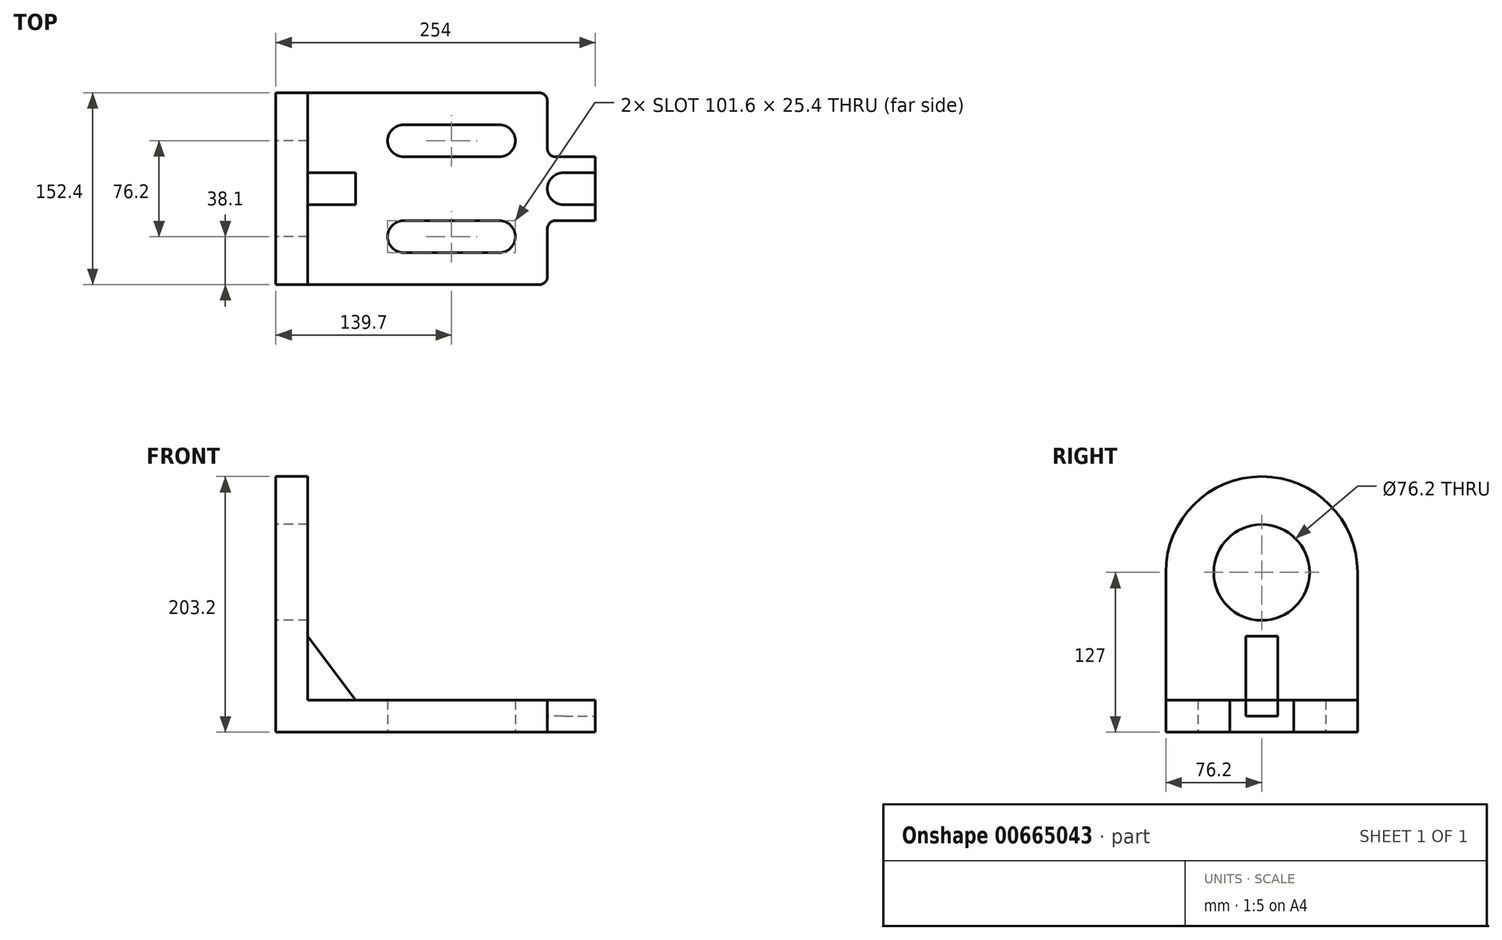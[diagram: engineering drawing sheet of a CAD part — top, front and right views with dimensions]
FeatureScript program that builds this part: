
annotation { "Feature Type Name" : "Feature", "Feature Type Description" : "" }
export const myFeature = defineFeature(function(context is Context, id is Id, definition is map)
    precondition{}
    {
        {
            var Q0;
            Q0=qCreatedBy(makeId("Top.planeOp"),FACE);
            var sketch = newSketch(context, id + "F0", { "sketchPlane" : qUnion([Q0])});
            skLineSegment(sketch, "E0", {"start": v(0, 0) * mm, "end": v(209.55, 0) * mm});
            skLineSegment(sketch, "E1", {"start": v(215.9, -6.35) * mm, "end": v(215.9, -44.45) * mm});
            skLineSegment(sketch, "E2", {"start": v(222.25, -50.8) * mm, "end": v(254, -50.8) * mm});
            skLineSegment(sketch, "E3", {"start": v(254, -50.8) * mm, "end": v(254, -63.5) * mm});
            skLineSegment(sketch, "E4", {"start": v(254, -63.5) * mm, "end": v(228.6, -63.5) * mm});
            skLineSegment(sketch, "E5", {"start": v(215.9, -76.2) * mm, "end": v(215.9, -76.2) * mm});
            skLineSegment(sketch, "E6", {"start": v(228.6, -88.9) * mm, "end": v(254, -88.9) * mm});
            skLineSegment(sketch, "E7", {"start": v(254, -88.9) * mm, "end": v(254, -101.6) * mm});
            skLineSegment(sketch, "E8", {"start": v(254, -101.6) * mm, "end": v(222.25, -101.6) * mm});
            skLineSegment(sketch, "E9", {"start": v(215.9, -107.95) * mm, "end": v(215.9, -146.05) * mm});
            skLineSegment(sketch, "E10", {"start": v(209.55, -152.4) * mm, "end": v(0, -152.4) * mm});
            skLineSegment(sketch, "E11", {"start": v(0, -152.4) * mm, "end": v(0, 0) * mm});
            skPoint(sketch, "E12.visualSharp", {"position": v(215.9, 0) * mm});
            skArc(sketch, "E12.filletArc", {"start": v(215.9, -6.35) * mm, "mid": v(214.04, -1.86) * mm, "end": v(209.55, 0) * mm});
            skPoint(sketch, "E13.visualSharp", {"position": v(215.9, -152.4) * mm});
            skArc(sketch, "E13.filletArc", {"start": v(209.55, -152.4) * mm, "mid": v(214.04, -150.54) * mm, "end": v(215.9, -146.05) * mm});
            skPoint(sketch, "E14.visualSharp", {"position": v(215.9, -50.8) * mm});
            skArc(sketch, "E14.filletArc", {"start": v(215.9, -44.45) * mm, "mid": v(217.76, -48.94) * mm, "end": v(222.25, -50.8) * mm});
            skPoint(sketch, "E15.visualSharp", {"position": v(215.9, -101.6) * mm});
            skArc(sketch, "E15.filletArc", {"start": v(222.25, -101.6) * mm, "mid": v(217.76, -103.46) * mm, "end": v(215.9, -107.95) * mm});
            skPoint(sketch, "E16.visualSharp", {"position": v(215.9, -63.5) * mm});
            skArc(sketch, "E16.filletArc", {"start": v(228.6, -63.5) * mm, "mid": v(219.62, -67.22) * mm, "end": v(215.9, -76.2) * mm});
            skPoint(sketch, "E17.visualSharp", {"position": v(215.9, -88.9) * mm});
            skArc(sketch, "E17.filletArc", {"start": v(215.9, -76.2) * mm, "mid": v(219.62, -85.18) * mm, "end": v(228.6, -88.9) * mm});
            skLineSegment(sketch, "E18", {"start": v(254, -63.5) * mm, "end": v(254, -88.9) * mm});
            skLineSegment(sketch, "E19.0", {"start": v(0, -38.1) * mm, "end": v(215.9, -38.1) * mm});
            skLineSegment(sketch, "E20.0", {"start": v(215.9, -114.3) * mm, "end": v(0, -114.3) * mm});
            skLineSegment(sketch, "E21.0", {"start": v(101.6, -50.8) * mm, "end": v(177.8, -50.8) * mm});
            skLineSegment(sketch, "E22.0", {"start": v(101.6, -25.4) * mm, "end": v(177.8, -25.4) * mm});
            skLineSegment(sketch, "E23.0", {"start": v(177.8, -101.6) * mm, "end": v(101.6, -101.6) * mm});
            skLineSegment(sketch, "E24.0", {"start": v(177.8, -127) * mm, "end": v(101.6, -127) * mm});
            skLineSegment(sketch, "E25.0", {"start": v(190.5, -38.1) * mm, "end": v(190.5, -38.1) * mm});
            skLineSegment(sketch, "E26.0", {"start": v(190.5, -114.3) * mm, "end": v(190.5, -114.3) * mm});
            skLineSegment(sketch, "E27.0", {"start": v(88.9, -38.1) * mm, "end": v(88.9, -38.1) * mm});
            skArc(sketch, "E28.filletArc", {"start": v(101.6, -25.4) * mm, "mid": v(92.62, -29.12) * mm, "end": v(88.9, -38.1) * mm});
            skArc(sketch, "E29.filletArc", {"start": v(88.9, -38.1) * mm, "mid": v(92.62, -47.08) * mm, "end": v(101.6, -50.8) * mm});
            skArc(sketch, "E30.filletArc", {"start": v(190.5, -38.1) * mm, "mid": v(186.78, -29.12) * mm, "end": v(177.8, -25.4) * mm});
            skPoint(sketch, "E31.visualSharp", {"position": v(190.5, -50.8) * mm});
            skArc(sketch, "E31.filletArc", {"start": v(177.8, -50.8) * mm, "mid": v(186.78, -47.08) * mm, "end": v(190.5, -38.1) * mm});
            skPoint(sketch, "E32.visualSharp", {"position": v(190.5, -101.6) * mm});
            skArc(sketch, "E32.filletArc", {"start": v(190.5, -114.3) * mm, "mid": v(186.78, -105.32) * mm, "end": v(177.8, -101.6) * mm});
            skArc(sketch, "E33.filletArc", {"start": v(177.8, -127) * mm, "mid": v(186.78, -123.28) * mm, "end": v(190.5, -114.3) * mm});
            skLineSegment(sketch, "E34", {"start": v(88.9, -114.3) * mm, "end": v(88.9, -114.3) * mm});
            skArc(sketch, "E35.filletArc", {"start": v(101.6, -101.6) * mm, "mid": v(92.62, -105.32) * mm, "end": v(88.9, -114.3) * mm});
            skArc(sketch, "E36.filletArc", {"start": v(88.9, -114.3) * mm, "mid": v(92.62, -123.28) * mm, "end": v(101.6, -127) * mm});
            skSolve(sketch);
        }
        {
            var Q0;
            Q0=makeQuery(id+"F0.imprint","IMPRINT",FACE,{"disambiguationData":[TD([[makeQuery(id+"F0.imprint","IMPRINT",EDGE,{"derivedFrom":sQuery(id+"F0.wireOp",EDGE,"E2")}),-1.0]])]});
            var Q1;
            {var subQ1=sQuery(id+"F0.wireOp",EDGE,"E0");Q1=makeQuery(id+"F0.imprint","IMPRINT",FACE,{"disambiguationData":[TD([[makeQuery(id+"F0.imprint","IMPRINT",EDGE,{"derivedFrom":subQ1}),-1.0]])]});}
            var Q2;
            {var subQ1=sQuery(id+"F0.wireOp",EDGE,"E10");Q2=makeQuery(id+"F0.imprint","IMPRINT",FACE,{"disambiguationData":[TD([[makeQuery(id+"F0.imprint","IMPRINT",EDGE,{"derivedFrom":subQ1}),-1.0]])]});}
            extrude(context, id + "F1", {"entities" : qUnion([Q0, Q1, Q2]), "depth" : 25.4 * mm, "offsetDistance" : 25.4 * mm});
        }
        {
            var Q0;
            Q0=makeQuery(id+"F0.imprint","IMPRINT",FACE,{"disambiguationData":[TD([[makeQuery(id+"F0.imprint","IMPRINT",EDGE,{"derivedFrom":sQuery(id+"F0.wireOp",EDGE,"E4")}),1.0]])]});
            extrude(context, id + "F2", {"entities" : qUnion([Q0]), "operationType" : NewBodyOperationType.ADD, "depth" : 12.7 * mm, "offsetDistance" : 25.4 * mm});
        }
        {
            var Q0;
            Q0=makeQuery(id+"F1.opExtrude","SWEPT_FACE",FACE,{"disambiguationData":[OSD([sQuery(id+"F0.wireOp",EDGE,"E11")])]});
            var sketch = newSketch(context, id + "F3", { "sketchPlane" : qUnion([Q0])});
            skLineSegment(sketch, "E37", {"start": v(0, 25.4) * mm, "end": v(0, 127) * mm});
            skLineSegment(sketch, "E38", {"start": v(76.2, 203.2) * mm, "end": v(76.2, 203.2) * mm});
            skLineSegment(sketch, "E39", {"start": v(152.4, 127) * mm, "end": v(152.4, 25.4) * mm});
            skPoint(sketch, "E40.visualSharp", {"position": v(0, 203.2) * mm});
            skArc(sketch, "E40.filletArc", {"start": v(76.2, 203.2) * mm, "mid": v(22.32, 180.88) * mm, "end": v(0, 127) * mm});
            skPoint(sketch, "E41.visualSharp", {"position": v(152.4, 203.2) * mm});
            skArc(sketch, "E41.filletArc", {"start": v(152.4, 127) * mm, "mid": v(130.08, 180.88) * mm, "end": v(76.2, 203.2) * mm});
            skCircle(sketch, "E42", {"center": v(76.2, 127) * mm, "radius": 38.1 * mm});
            skSolve(sketch);
        }
        {
            var Q0;
            Q0=makeQuery(id+"F3.imprint","IMPRINT",FACE,{"disambiguationData":[TD([[makeQuery(id+"F3.imprint","IMPRINT",EDGE,{"derivedFrom":sQuery(id+"F3.wireOp",EDGE,"E37")}),-1.0]])]});
            extrude(context, id + "F4", {"entities" : qUnion([Q0]), "operationType" : NewBodyOperationType.ADD, "oppositeDirection" : true, "depth" : 25.4 * mm, "offsetDistance" : 25.4 * mm});
        }
        {
            var Q0;
            Q0=makeQuery(id+"F4.boolean.opBoolean","MERGE",FACE,{"derivedFrom":[makeQuery(id+"F1.opExtrude","SWEPT_FACE",FACE,{"disambiguationData":[OSD([sQuery(id+"F0.wireOp",EDGE,"E10")])]}),makeQuery(id+"F4.opExtrude","SWEPT_FACE",FACE,{"disambiguationData":[OSD([sQuery(id+"F3.wireOp",EDGE,"E39")])]})]});
            var sketch = newSketch(context, id + "F5", { "sketchPlane" : qUnion([Q0])});
            skLineSegment(sketch, "E43", {"start": v(25.4, 25.4) * mm, "end": v(25.4, 76.2) * mm});
            skLineSegment(sketch, "E44", {"start": v(25.4, 25.4) * mm, "end": v(63.5, 25.4) * mm});
            skLineSegment(sketch, "E45", {"start": v(63.5, 25.4) * mm, "end": v(25.4, 76.2) * mm});
            skSolve(sketch);
        }
        {
            var Q0;
            Q0=makeQuery(id+"F5.imprint","IMPRINT",FACE,{"disambiguationData":[TD([[makeQuery(id+"F5.imprint","IMPRINT",EDGE,{"derivedFrom":sQuery(id+"F5.wireOp",EDGE,"E43")}),1.0]])]});
            extrude(context, id + "F6", {"entities" : qUnion([Q0]), "operationType" : NewBodyOperationType.ADD, "oppositeDirection" : true, "depth" : 88.9 * mm, "offsetDistance" : 25.4 * mm, "hasSecondDirection" : true, "secondDirectionOppositeDirection" : true, "secondDirectionDepth" : 63.5 * mm});
        }
    });
